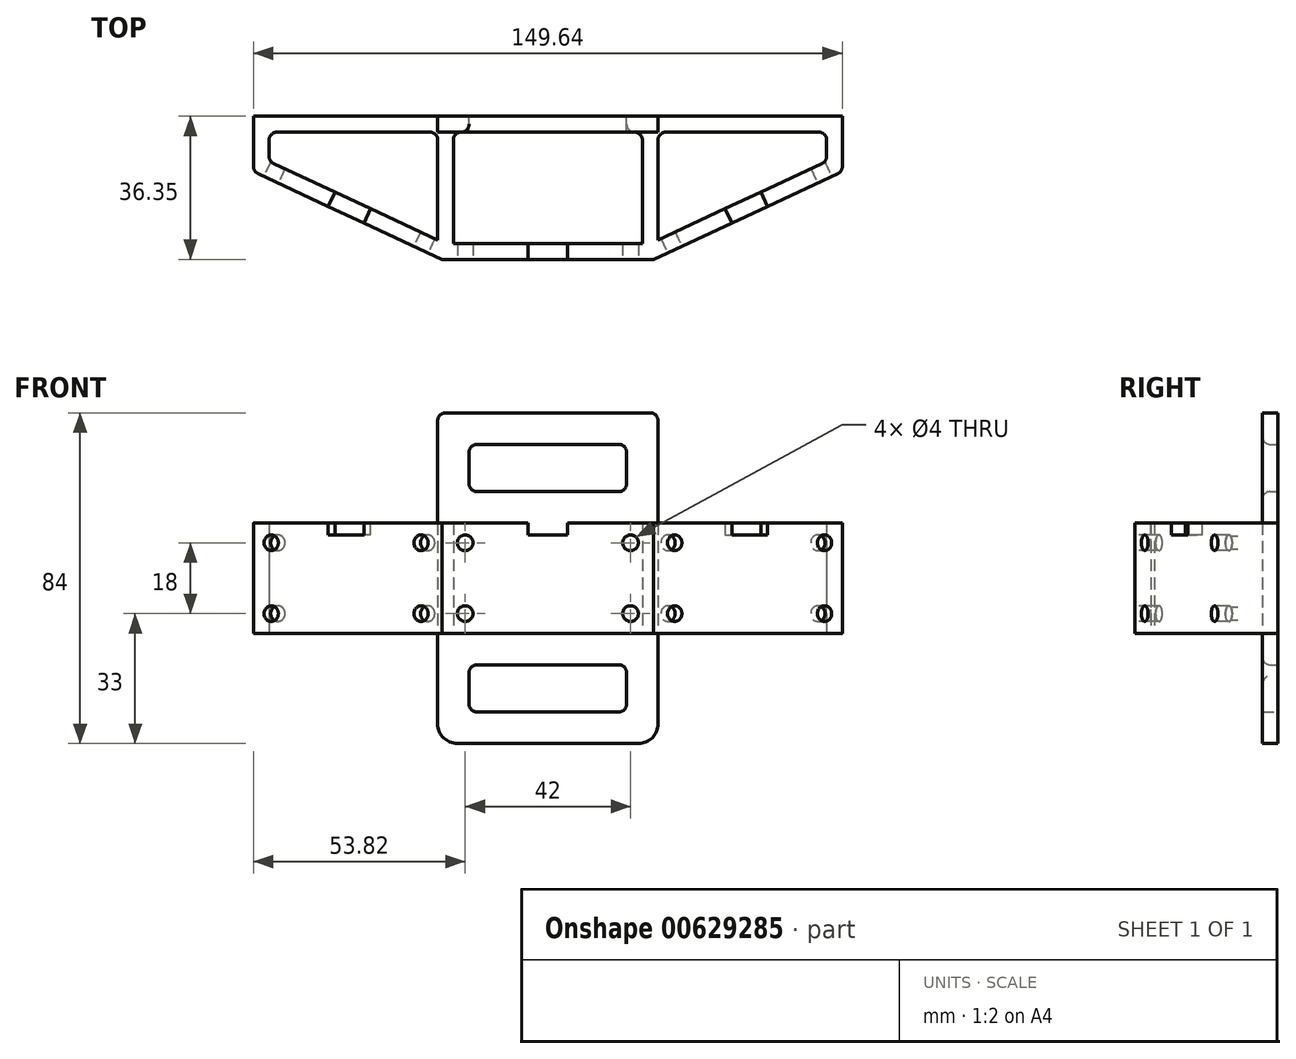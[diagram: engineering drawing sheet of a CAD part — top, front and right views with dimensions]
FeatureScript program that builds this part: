
annotation { "Feature Type Name" : "Feature", "Feature Type Description" : "" }
export const myFeature = defineFeature(function(context is Context, id is Id, definition is map)
    precondition{}
    {
        {
            var Q0;
            Q0=qCreatedBy(makeId("Top.planeOp"),FACE);
            var sketch = newSketch(context, id + "F0", { "sketchPlane" : qUnion([Q0])});
            skLineSegment(sketch, "E0", {"start": v(24, -117.28) * mm, "end": v(0, -117.28) * mm});
            skLineSegment(sketch, "E1", {"start": v(-28, -116.35) * mm, "end": v(-70.82, -96.38) * mm});
            skLineSegment(sketch, "E2", {"start": v(28, -116.35) * mm, "end": v(70.82, -96.38) * mm});
            skPoint(sketch, "E3.endSnap0", {"position": v(0, -117.28) * mm});
            skLineSegment(sketch, "E4", {"start": v(74.82, -98.93) * mm, "end": v(26.89, -121.28) * mm});
            skLineSegment(sketch, "E5", {"start": v(0, -121.28) * mm, "end": v(26.89, -121.28) * mm});
            skLineSegment(sketch, "E6", {"start": v(0, -121.28) * mm, "end": v(-26.89, -121.28) * mm});
            skLineSegment(sketch, "E7", {"start": v(-74.82, -98.93) * mm, "end": v(-26.89, -121.28) * mm});
            skPoint(sketch, "E3.start.orphan", {"position": v(0, -117.28) * mm});
            skLineSegment(sketch, "E8", {"start": v(74.82, -98.93) * mm, "end": v(74.82, -88.93) * mm});
            skLineSegment(sketch, "E9", {"start": v(70.82, -88.93) * mm, "end": v(70.82, -96.38) * mm});
            skLineSegment(sketch, "E10", {"start": v(-74.82, -98.93) * mm, "end": v(-74.82, -88.93) * mm});
            skLineSegment(sketch, "E11", {"start": v(-70.82, -88.93) * mm, "end": v(-70.82, -96.38) * mm});
            skLineSegment(sketch, "E12", {"start": v(-74.82, -88.93) * mm, "end": v(-74.82, -84.93) * mm});
            skLineSegment(sketch, "E13", {"start": v(74.82, -88.93) * mm, "end": v(74.82, -84.93) * mm});
            skLineSegment(sketch, "E14", {"start": v(74.82, -84.93) * mm, "end": v(-74.82, -84.93) * mm});
            skLineSegment(sketch, "E15", {"start": v(-26, -84.93) * mm, "end": v(-24, -84.93) * mm});
            skLineSegment(sketch, "E16", {"start": v(-24, -88.93) * mm, "end": v(-24, -117.28) * mm});
            skLineSegment(sketch, "E17", {"start": v(-26, -84.93) * mm, "end": v(-28, -84.93) * mm});
            skLineSegment(sketch, "E18", {"start": v(-28, -88.93) * mm, "end": v(-28, -116.35) * mm});
            skLineSegment(sketch, "E19", {"start": v(26, -84.93) * mm, "end": v(28, -84.93) * mm});
            skLineSegment(sketch, "E20", {"start": v(28, -88.93) * mm, "end": v(28, -116.35) * mm});
            skLineSegment(sketch, "E21", {"start": v(26, -84.93) * mm, "end": v(24, -84.93) * mm});
            skLineSegment(sketch, "E22", {"start": v(24, -88.93) * mm, "end": v(24, -117.28) * mm});
            skLineSegment(sketch, "E23.trimOffspring", {"start": v(28, -88.93) * mm, "end": v(70.82, -88.93) * mm});
            skLineSegment(sketch, "E24", {"start": v(24, -88.93) * mm, "end": v(-24, -88.93) * mm});
            skPoint(sketch, "E25.orphan", {"position": v(26, -117.28) * mm});
            skLineSegment(sketch, "E26", {"start": v(-28, -88.93) * mm, "end": v(-70.82, -88.93) * mm});
            skPoint(sketch, "E27.orphan", {"position": v(-26, -117.28) * mm});
            skLineSegment(sketch, "E28", {"start": v(0, -117.28) * mm, "end": v(-24, -117.28) * mm});
            skSolve(sketch);
        }
        {
            var Q0;
            Q0 = qSketchRegion(id + "F0", true);
            extrude(context, id + "F1", {"entities" : qUnion([Q0]), "depth" : 28 * mm, "offsetDistance" : 25 * mm});
        }
        {
            var Q0;
            Q0=makeQuery(id+"F1.opExtrude","CAP_FACE",FACE,{"disambiguationData":[OSD([sQuery(id+"F0.wireOp",EDGE,"E0"),sQuery(id+"F0.wireOp",EDGE,"E1"),sQuery(id+"F0.wireOp",EDGE,"E2"),sQuery(id+"F0.wireOp",EDGE,"E4"),sQuery(id+"F0.wireOp",EDGE,"E5"),sQuery(id+"F0.wireOp",EDGE,"E6"),sQuery(id+"F0.wireOp",EDGE,"E7"),sQuery(id+"F0.wireOp",EDGE,"E8"),sQuery(id+"F0.wireOp",EDGE,"E9"),sQuery(id+"F0.wireOp",EDGE,"E10"),sQuery(id+"F0.wireOp",EDGE,"E11"),sQuery(id+"F0.wireOp",EDGE,"E12"),sQuery(id+"F0.wireOp",EDGE,"E13"),sQuery(id+"F0.wireOp",EDGE,"E14"),sQuery(id+"F0.wireOp",EDGE,"E15"),sQuery(id+"F0.wireOp",EDGE,"E16"),sQuery(id+"F0.wireOp",EDGE,"E17"),sQuery(id+"F0.wireOp",EDGE,"E18"),sQuery(id+"F0.wireOp",EDGE,"E19"),sQuery(id+"F0.wireOp",EDGE,"E20"),sQuery(id+"F0.wireOp",EDGE,"E21"),sQuery(id+"F0.wireOp",EDGE,"E22"),sQuery(id+"F0.wireOp",EDGE,"E23.trimOffspring"),sQuery(id+"F0.wireOp",EDGE,"E24"),sQuery(id+"F0.wireOp",EDGE,"E26"),sQuery(id+"F0.wireOp",EDGE,"E28")])],"isStart":false});
            var sketch = newSketch(context, id + "F2", { "sketchPlane" : qUnion([Q0])});
            skLineSegment(sketch, "E29", {"start": v(28, -88.93) * mm, "end": v(28, -84.93) * mm});
            skLineSegment(sketch, "E30", {"start": v(-28, -88.93) * mm, "end": v(-28, -84.93) * mm});
            skLineSegment(sketch, "E31", {"start": v(-28, -84.93) * mm, "end": v(28, -84.93) * mm});
            skLineSegment(sketch, "E32", {"start": v(-28, -88.93) * mm, "end": v(28, -88.93) * mm});
            skSolve(sketch);
        }
        {
            var Q0;
            Q0 = qSketchRegion(id + "F2", true);
            extrude(context, id + "F3", {"entities" : qUnion([Q0]), "operationType" : NewBodyOperationType.ADD, "depth" : 28 * mm, "offsetDistance" : 25 * mm});
        }
        {
            var Q0;
            Q0=makeQuery(id+"F1.opExtrude","CAP_FACE",FACE,{"disambiguationData":[OSD([sQuery(id+"F0.wireOp",EDGE,"E0"),sQuery(id+"F0.wireOp",EDGE,"E1"),sQuery(id+"F0.wireOp",EDGE,"E2"),sQuery(id+"F0.wireOp",EDGE,"E4"),sQuery(id+"F0.wireOp",EDGE,"E5"),sQuery(id+"F0.wireOp",EDGE,"E6"),sQuery(id+"F0.wireOp",EDGE,"E7"),sQuery(id+"F0.wireOp",EDGE,"E8"),sQuery(id+"F0.wireOp",EDGE,"E9"),sQuery(id+"F0.wireOp",EDGE,"E10"),sQuery(id+"F0.wireOp",EDGE,"E11"),sQuery(id+"F0.wireOp",EDGE,"E12"),sQuery(id+"F0.wireOp",EDGE,"E13"),sQuery(id+"F0.wireOp",EDGE,"E14"),sQuery(id+"F0.wireOp",EDGE,"E15"),sQuery(id+"F0.wireOp",EDGE,"E16"),sQuery(id+"F0.wireOp",EDGE,"E17"),sQuery(id+"F0.wireOp",EDGE,"E18"),sQuery(id+"F0.wireOp",EDGE,"E19"),sQuery(id+"F0.wireOp",EDGE,"E20"),sQuery(id+"F0.wireOp",EDGE,"E21"),sQuery(id+"F0.wireOp",EDGE,"E22"),sQuery(id+"F0.wireOp",EDGE,"E23.trimOffspring"),sQuery(id+"F0.wireOp",EDGE,"E24"),sQuery(id+"F0.wireOp",EDGE,"E26"),sQuery(id+"F0.wireOp",EDGE,"E28")])],"isStart":true});
            var sketch = newSketch(context, id + "F4", { "sketchPlane" : qUnion([Q0])});
            skLineSegment(sketch, "E33", {"start": v(-28, 88.93) * mm, "end": v(-28, 84.93) * mm});
            skLineSegment(sketch, "E34", {"start": v(28, 88.93) * mm, "end": v(28, 84.93) * mm});
            skLineSegment(sketch, "E35", {"start": v(28, 84.93) * mm, "end": v(-28, 84.93) * mm});
            skLineSegment(sketch, "E36", {"start": v(28, 88.93) * mm, "end": v(-28, 88.93) * mm});
            skSolve(sketch);
        }
        {
            var Q0;
            Q0 = qSketchRegion(id + "F4", true);
            extrude(context, id + "F5", {"entities" : qUnion([Q0]), "operationType" : NewBodyOperationType.ADD, "depth" : 28 * mm, "offsetDistance" : 25 * mm});
        }
        {
            var Q0;
            Q0=makeQuery(id+"F5.boolean.opBoolean","MERGE",FACE,{"derivedFrom":[makeQuery(id+"F3.boolean.opBoolean","MERGE",FACE,{"derivedFrom":[makeQuery(id+"F1.opExtrude","SWEPT_FACE",FACE,{"disambiguationData":[OSD([sQuery(id+"F0.wireOp",EDGE,"E14"),sQuery(id+"F0.wireOp",EDGE,"E15"),sQuery(id+"F0.wireOp",EDGE,"E17"),sQuery(id+"F0.wireOp",EDGE,"E19"),sQuery(id+"F0.wireOp",EDGE,"E21")])]}),makeQuery(id+"F3.opExtrude","SWEPT_FACE",FACE,{"disambiguationData":[OSD([sQuery(id+"F2.wireOp",EDGE,"E31")])]})]}),makeQuery(id+"F5.opExtrude","SWEPT_FACE",FACE,{"disambiguationData":[OSD([sQuery(id+"F4.wireOp",EDGE,"E35")])]})]});
            var sketch = newSketch(context, id + "F6", { "sketchPlane" : qUnion([Q0])});
            skLineSegment(sketch, "E37", {"start": v(0, -28) * mm, "end": v(0, -20) * mm});
            skLineSegment(sketch, "E38", {"start": v(0, -20) * mm, "end": v(20, -20) * mm});
            skLineSegment(sketch, "E39", {"start": v(20, -20) * mm, "end": v(20, -8) * mm});
            skLineSegment(sketch, "E40", {"start": v(20, -8) * mm, "end": v(-20, -8) * mm});
            skLineSegment(sketch, "E41", {"start": v(-20, -8) * mm, "end": v(-20, -20) * mm});
            skLineSegment(sketch, "E42", {"start": v(0, -20) * mm, "end": v(-20, -20) * mm});
            skLineSegment(sketch, "E43", {"start": v(0, 56) * mm, "end": v(0, 48) * mm});
            skPoint(sketch, "E43.endSnap0", {"position": v(0, 56) * mm});
            skLineSegment(sketch, "E44", {"start": v(0, 48) * mm, "end": v(-20, 48) * mm});
            skLineSegment(sketch, "E45", {"start": v(-20, 48) * mm, "end": v(-20, 36) * mm});
            skLineSegment(sketch, "E46", {"start": v(-20, 36) * mm, "end": v(20, 36) * mm});
            skLineSegment(sketch, "E47", {"start": v(20, 36) * mm, "end": v(20, 48) * mm});
            skLineSegment(sketch, "E48", {"start": v(20, 48) * mm, "end": v(0, 48) * mm});
            skSolve(sketch);
        }
        {
            var Q0;
            Q0=makeQuery(id+"F6.imprint","IMPRINT",FACE,{"disambiguationData":[TD([[makeQuery(id+"F6.imprint","IMPRINT",EDGE,{"derivedFrom":sQuery(id+"F6.wireOp",EDGE,"E38")}),1.0]])]});
            var Q1;
            Q1=makeQuery(id+"F6.imprint","IMPRINT",FACE,{"disambiguationData":[TD([[makeQuery(id+"F6.imprint","IMPRINT",EDGE,{"derivedFrom":sQuery(id+"F6.wireOp",EDGE,"E44")}),1.0]])]});
            extrude(context, id + "F7", {"entities" : qUnion([Q0, Q1]), "operationType" : NewBodyOperationType.REMOVE, "oppositeDirection" : true, "depth" : 25 * mm, "offsetDistance" : 25 * mm});
        }
        {
            var Q0;
            Q0=makeQuery(id+"F1.opExtrude","SWEPT_FACE",FACE,{"disambiguationData":[OSD([sQuery(id+"F0.wireOp",EDGE,"E5"),sQuery(id+"F0.wireOp",EDGE,"E6")])]});
            var sketch = newSketch(context, id + "F8", { "sketchPlane" : qUnion([Q0])});
            skLineSegment(sketch, "E49", {"start": v(0, 0) * mm, "end": v(0, 28) * mm});
            skLineSegment(sketch, "E50", {"start": v(0, 14) * mm, "end": v(21, 14) * mm});
            skLineSegment(sketch, "E51", {"start": v(21, 14) * mm, "end": v(21, 23) * mm});
            skLineSegment(sketch, "E52", {"start": v(21, 14) * mm, "end": v(21, 5) * mm});
            skLineSegment(sketch, "E53", {"start": v(0, 14) * mm, "end": v(-21, 14) * mm});
            skLineSegment(sketch, "E54", {"start": v(-21, 14) * mm, "end": v(-21, 23) * mm});
            skLineSegment(sketch, "E55", {"start": v(-21, 14) * mm, "end": v(-21, 5) * mm});
            skLineSegment(sketch, "E56", {"start": v(0, 28) * mm, "end": v(-5, 28) * mm});
            skLineSegment(sketch, "E57", {"start": v(-5, 28) * mm, "end": v(-5, 25) * mm});
            skLineSegment(sketch, "E58", {"start": v(-5, 25) * mm, "end": v(5, 25) * mm});
            skLineSegment(sketch, "E59", {"start": v(5, 25) * mm, "end": v(5, 28) * mm});
            skCircle(sketch, "E60", {"center": v(-21, 23) * mm, "radius": 2 * mm});
            skCircle(sketch, "E61", {"center": v(-21, 5) * mm, "radius": 2 * mm});
            skCircle(sketch, "E62", {"center": v(21, 23) * mm, "radius": 2 * mm});
            skCircle(sketch, "E63", {"center": v(21, 5) * mm, "radius": 2 * mm});
            skSolve(sketch);
        }
        {
            var Q0;
            Q0 = qSketchRegion(id + "F8", true);
            var Q1;
            {var subQ5=sQuery(id+"F8.wireOp",EDGE,"E59");Q1=makeQuery(id+"F8.imprint","IMPRINT",FACE,{"disambiguationData":[TD([[makeQuery(id+"F8.imprint","IMPRINT",EDGE,{"derivedFrom":subQ5}),1.0]])]});}
            extrude(context, id + "F9", {"entities" : qUnion([Q0, Q1]), "operationType" : NewBodyOperationType.REMOVE, "oppositeDirection" : true, "depth" : 25 * mm, "offsetDistance" : 25 * mm});
        }
        {
            var Q0;
            Q0=makeQuery(id+"F1.opExtrude","SWEPT_FACE",FACE,{"disambiguationData":[OSD([sQuery(id+"F0.wireOp",EDGE,"E4")])]});
            var sketch = newSketch(context, id + "F10", { "sketchPlane" : qUnion([Q0])});
            skLineSegment(sketch, "E64", {"start": v(0, 0) * mm, "end": v(0, 28) * mm});
            skLineSegment(sketch, "E65", {"start": v(0, 28) * mm, "end": v(-5, 28) * mm});
            skLineSegment(sketch, "E66", {"start": v(-5, 28) * mm, "end": v(-5, 25) * mm});
            skLineSegment(sketch, "E67", {"start": v(-5, 25) * mm, "end": v(5, 25) * mm});
            skLineSegment(sketch, "E68", {"start": v(5, 25) * mm, "end": v(5, 28) * mm});
            skLineSegment(sketch, "E69", {"start": v(0, 14) * mm, "end": v(-21, 14) * mm});
            skPoint(sketch, "E69.endSnap0", {"position": v(0, 14) * mm});
            skLineSegment(sketch, "E70", {"start": v(-21, 14) * mm, "end": v(-21, 23) * mm});
            skLineSegment(sketch, "E71", {"start": v(-21, 14) * mm, "end": v(-21, 5) * mm});
            skLineSegment(sketch, "E72", {"start": v(0, 14) * mm, "end": v(21, 14) * mm});
            skLineSegment(sketch, "E73", {"start": v(21, 14) * mm, "end": v(21, 23) * mm});
            skLineSegment(sketch, "E74", {"start": v(21, 14) * mm, "end": v(21, 5) * mm});
            skCircle(sketch, "E75", {"center": v(-21, 23) * mm, "radius": 2 * mm});
            skCircle(sketch, "E76", {"center": v(-21, 5) * mm, "radius": 2 * mm});
            skCircle(sketch, "E77", {"center": v(21, 23) * mm, "radius": 2 * mm});
            skCircle(sketch, "E78", {"center": v(21, 5) * mm, "radius": 2 * mm});
            skSolve(sketch);
        }
        {
            var Q0;
            Q0 = qSketchRegion(id + "F10", true);
            var Q1;
            {var subQ5=sQuery(id+"F10.wireOp",EDGE,"E68");Q1=makeQuery(id+"F10.imprint","IMPRINT",FACE,{"disambiguationData":[TD([[makeQuery(id+"F10.imprint","IMPRINT",EDGE,{"derivedFrom":subQ5}),1.0]])]});}
            extrude(context, id + "F11", {"entities" : qUnion([Q0, Q1]), "operationType" : NewBodyOperationType.REMOVE, "oppositeDirection" : true, "depth" : 4 * mm, "offsetDistance" : 25 * mm});
        }
        {
            var Q0;
            Q0=makeQuery(id+"F1.opExtrude","SWEPT_FACE",FACE,{"disambiguationData":[OSD([sQuery(id+"F0.wireOp",EDGE,"E7")])]});
            var sketch = newSketch(context, id + "F12", { "sketchPlane" : qUnion([Q0])});
            skLineSegment(sketch, "E79", {"start": v(-26, 14) * mm, "end": v(26.89, 14) * mm});
            skLineSegment(sketch, "E80", {"start": v(0, 14) * mm, "end": v(0, 28) * mm});
            skLineSegment(sketch, "E81", {"start": v(0, 14) * mm, "end": v(0, 5) * mm});
            skLineSegment(sketch, "E82", {"start": v(0, 5) * mm, "end": v(21, 5) * mm});
            skLineSegment(sketch, "E83", {"start": v(0, 5) * mm, "end": v(-21, 5) * mm});
            skLineSegment(sketch, "E84", {"start": v(0, 14) * mm, "end": v(0, 23) * mm});
            skLineSegment(sketch, "E85", {"start": v(0, 23) * mm, "end": v(21, 23) * mm});
            skLineSegment(sketch, "E86", {"start": v(0, 23) * mm, "end": v(-21, 23) * mm});
            skLineSegment(sketch, "E87", {"start": v(0, 28) * mm, "end": v(-5, 28) * mm});
            skLineSegment(sketch, "E88", {"start": v(-5, 28) * mm, "end": v(-5, 25) * mm});
            skLineSegment(sketch, "E89", {"start": v(-5, 25) * mm, "end": v(5, 25) * mm});
            skLineSegment(sketch, "E90", {"start": v(5, 25) * mm, "end": v(5, 28) * mm});
            skCircle(sketch, "E91", {"center": v(-21, 23) * mm, "radius": 2 * mm});
            skCircle(sketch, "E92", {"center": v(-21, 5) * mm, "radius": 2 * mm});
            skCircle(sketch, "E93", {"center": v(21, 23) * mm, "radius": 2 * mm});
            skCircle(sketch, "E94", {"center": v(21, 5) * mm, "radius": 2 * mm});
            skSolve(sketch);
        }
        {
            var Q0;
            Q0=makeQuery(id+"F12.imprint","IMPRINT",FACE,{"disambiguationData":[TD([[makeQuery(id+"F12.imprint","IMPRINT",EDGE,{"derivedFrom":sQuery(id+"F12.wireOp",EDGE,"E92")}),1.0]])]});
            var Q1;
            Q1=makeQuery(id+"F12.imprint","IMPRINT",FACE,{"disambiguationData":[TD([[makeQuery(id+"F12.imprint","IMPRINT",EDGE,{"derivedFrom":sQuery(id+"F12.wireOp",EDGE,"E93")}),1.0]])]});
            var Q2;
            Q2=makeQuery(id+"F12.imprint","IMPRINT",FACE,{"disambiguationData":[TD([[makeQuery(id+"F12.imprint","IMPRINT",EDGE,{"derivedFrom":sQuery(id+"F12.wireOp",EDGE,"E94")}),1.0]])]});
            var Q3;
            {var subQ0=sQuery(id+"F12.wireOp",EDGE,"E87");Q3=makeQuery(id+"F12.imprint","IMPRINT",FACE,{"disambiguationData":[TD([[makeQuery(id+"F12.imprint","IMPRINT",EDGE,{"derivedFrom":subQ0}),-1.0]])]});}
            var Q4;
            {var subQ5=sQuery(id+"F12.wireOp",EDGE,"E90");Q4=makeQuery(id+"F12.imprint","IMPRINT",FACE,{"disambiguationData":[TD([[makeQuery(id+"F12.imprint","IMPRINT",EDGE,{"derivedFrom":subQ5}),1.0]])]});}
            var Q5;
            Q5=makeQuery(id+"F12.imprint","IMPRINT",FACE,{"disambiguationData":[TD([[makeQuery(id+"F12.imprint","IMPRINT",EDGE,{"derivedFrom":sQuery(id+"F12.wireOp",EDGE,"E91")}),1.0]])]});
            extrude(context, id + "F13", {"entities" : qUnion([Q0, Q1, Q2, Q3, Q4, Q5]), "operationType" : NewBodyOperationType.REMOVE, "oppositeDirection" : true, "depth" : 4 * mm, "offsetDistance" : 25 * mm});
        }
        {
            var Q0;
            Q0=makeQuery(id+"F7.boolean.opBoolean","INTERSECT",EDGE,{"derivedFrom":[makeQuery(id+"F5.boolean.opBoolean","MERGE",FACE,{"derivedFrom":[makeQuery(id+"F3.boolean.opBoolean","MERGE",FACE,{"derivedFrom":[makeQuery(id+"F1.opExtrude","SWEPT_FACE",FACE,{"disambiguationData":[OSD([sQuery(id+"F0.wireOp",EDGE,"E24")])]}),makeQuery(id+"F3.opExtrude","SWEPT_FACE",FACE,{"disambiguationData":[OSD([sQuery(id+"F2.wireOp",EDGE,"E32")])]})]}),makeQuery(id+"F5.opExtrude","SWEPT_FACE",FACE,{"disambiguationData":[OSD([sQuery(id+"F4.wireOp",EDGE,"E36")])]})]}),makeQuery(id+"F7.opExtrude","SWEPT_FACE",FACE,{"disambiguationData":[OSD([sQuery(id+"F6.wireOp",EDGE,"E46")])]})]});
            var Q1;
            Q1=makeQuery(id+"F7.boolean.opBoolean","COPY",EDGE,{"derivedFrom":makeQuery(id+"F7.opExtrude","CAP_EDGE",EDGE,{"disambiguationData":[OSD([sQuery(id+"F6.wireOp",EDGE,"E46")])],"isStart":true})});
            var Q2;
            Q2=makeQuery(id+"F7.boolean.opBoolean","INTERSECT",EDGE,{"derivedFrom":[makeQuery(id+"F5.boolean.opBoolean","MERGE",FACE,{"derivedFrom":[makeQuery(id+"F3.boolean.opBoolean","MERGE",FACE,{"derivedFrom":[makeQuery(id+"F1.opExtrude","SWEPT_FACE",FACE,{"disambiguationData":[OSD([sQuery(id+"F0.wireOp",EDGE,"E24")])]}),makeQuery(id+"F3.opExtrude","SWEPT_FACE",FACE,{"disambiguationData":[OSD([sQuery(id+"F2.wireOp",EDGE,"E32")])]})]}),makeQuery(id+"F5.opExtrude","SWEPT_FACE",FACE,{"disambiguationData":[OSD([sQuery(id+"F4.wireOp",EDGE,"E36")])]})]}),makeQuery(id+"F7.opExtrude","SWEPT_FACE",FACE,{"disambiguationData":[OSD([sQuery(id+"F6.wireOp",EDGE,"E47")])]})]});
            var Q3;
            Q3=makeQuery(id+"F7.boolean.opBoolean","COPY",EDGE,{"derivedFrom":makeQuery(id+"F7.opExtrude","CAP_EDGE",EDGE,{"disambiguationData":[OSD([sQuery(id+"F6.wireOp",EDGE,"E47")])],"isStart":true})});
            var Q4;
            Q4=makeQuery(id+"F7.boolean.opBoolean","COPY",EDGE,{"derivedFrom":makeQuery(id+"F7.opExtrude","CAP_EDGE",EDGE,{"disambiguationData":[OSD([sQuery(id+"F6.wireOp",EDGE,"E45")])],"isStart":true})});
            var Q5;
            Q5=makeQuery(id+"F7.boolean.opBoolean","INTERSECT",EDGE,{"derivedFrom":[makeQuery(id+"F5.boolean.opBoolean","MERGE",FACE,{"derivedFrom":[makeQuery(id+"F3.boolean.opBoolean","MERGE",FACE,{"derivedFrom":[makeQuery(id+"F1.opExtrude","SWEPT_FACE",FACE,{"disambiguationData":[OSD([sQuery(id+"F0.wireOp",EDGE,"E24")])]}),makeQuery(id+"F3.opExtrude","SWEPT_FACE",FACE,{"disambiguationData":[OSD([sQuery(id+"F2.wireOp",EDGE,"E32")])]})]}),makeQuery(id+"F5.opExtrude","SWEPT_FACE",FACE,{"disambiguationData":[OSD([sQuery(id+"F4.wireOp",EDGE,"E36")])]})]}),makeQuery(id+"F7.opExtrude","SWEPT_FACE",FACE,{"disambiguationData":[OSD([sQuery(id+"F6.wireOp",EDGE,"E45")])]})]});
            var Q6;
            Q6=makeQuery(id+"F7.boolean.opBoolean","COPY",EDGE,{"derivedFrom":makeQuery(id+"F7.opExtrude","SWEPT_EDGE",EDGE,{"disambiguationData":[OSD([sQuery(id+"F6.wireOp",EDGE,"E45"),sQuery(id+"F6.wireOp",EDGE,"E46")])]})});
            var Q7;
            Q7=makeQuery(id+"F7.boolean.opBoolean","COPY",EDGE,{"derivedFrom":makeQuery(id+"F7.opExtrude","SWEPT_EDGE",EDGE,{"disambiguationData":[OSD([sQuery(id+"F6.wireOp",EDGE,"E46"),sQuery(id+"F6.wireOp",EDGE,"E47")])]})});
            var Q8;
            Q8=makeQuery(id+"F7.boolean.opBoolean","COPY",EDGE,{"derivedFrom":makeQuery(id+"F7.opExtrude","SWEPT_EDGE",EDGE,{"disambiguationData":[OSD([sQuery(id+"F6.wireOp",EDGE,"E47"),sQuery(id+"F6.wireOp",EDGE,"E48")])]})});
            var Q9;
            Q9=makeQuery(id+"F7.boolean.opBoolean","INTERSECT",EDGE,{"derivedFrom":[makeQuery(id+"F5.boolean.opBoolean","MERGE",FACE,{"derivedFrom":[makeQuery(id+"F3.boolean.opBoolean","MERGE",FACE,{"derivedFrom":[makeQuery(id+"F1.opExtrude","SWEPT_FACE",FACE,{"disambiguationData":[OSD([sQuery(id+"F0.wireOp",EDGE,"E24")])]}),makeQuery(id+"F3.opExtrude","SWEPT_FACE",FACE,{"disambiguationData":[OSD([sQuery(id+"F2.wireOp",EDGE,"E32")])]})]}),makeQuery(id+"F5.opExtrude","SWEPT_FACE",FACE,{"disambiguationData":[OSD([sQuery(id+"F4.wireOp",EDGE,"E36")])]})]}),makeQuery(id+"F7.opExtrude","SWEPT_FACE",FACE,{"disambiguationData":[OSD([sQuery(id+"F6.wireOp",EDGE,"E44"),sQuery(id+"F6.wireOp",EDGE,"E48")])]})]});
            var Q10;
            Q10=makeQuery(id+"F7.boolean.opBoolean","COPY",EDGE,{"derivedFrom":makeQuery(id+"F7.opExtrude","CAP_EDGE",EDGE,{"disambiguationData":[OSD([sQuery(id+"F6.wireOp",EDGE,"E44"),sQuery(id+"F6.wireOp",EDGE,"E48")])],"isStart":true})});
            var Q11;
            Q11=makeQuery(id+"F7.boolean.opBoolean","COPY",EDGE,{"derivedFrom":makeQuery(id+"F7.opExtrude","SWEPT_EDGE",EDGE,{"disambiguationData":[OSD([sQuery(id+"F6.wireOp",EDGE,"E44"),sQuery(id+"F6.wireOp",EDGE,"E45")])]})});
            var Q12;
            Q12=makeQuery(id+"F3.opExtrude","CAP_EDGE",EDGE,{"disambiguationData":[OSD([sQuery(id+"F2.wireOp",EDGE,"E30")])],"isStart":false});
            var Q13;
            Q13=makeQuery(id+"F3.opExtrude","CAP_EDGE",EDGE,{"disambiguationData":[OSD([sQuery(id+"F2.wireOp",EDGE,"E29")])],"isStart":false});
            fillet(context, id + "F14", {"entities" : qUnion([Q0, Q1, Q2, Q3, Q4, Q5, Q6, Q7, Q8, Q9, Q10, Q11, Q12, Q13]), "radius" : 2 * mm, "tangentPropagation" : true, "allowEdgeOverflow" : false});
        }
        {
            var Q0;
            Q0=makeQuery(id+"F1.opExtrude","SWEPT_EDGE",EDGE,{"disambiguationData":[OSD([sQuery(id+"F0.wireOp",EDGE,"E20"),sQuery(id+"F0.wireOp",EDGE,"E23.trimOffspring")])]});
            var Q1;
            Q1=makeQuery(id+"F1.opExtrude","SWEPT_EDGE",EDGE,{"disambiguationData":[OSD([sQuery(id+"F0.wireOp",EDGE,"E22"),sQuery(id+"F0.wireOp",EDGE,"E24")])]});
            var Q2;
            Q2=makeQuery(id+"F1.opExtrude","SWEPT_EDGE",EDGE,{"disambiguationData":[OSD([sQuery(id+"F0.wireOp",EDGE,"E16"),sQuery(id+"F0.wireOp",EDGE,"E24")])]});
            var Q3;
            Q3=makeQuery(id+"F1.opExtrude","SWEPT_EDGE",EDGE,{"disambiguationData":[OSD([sQuery(id+"F0.wireOp",EDGE,"E18"),sQuery(id+"F0.wireOp",EDGE,"E26")])]});
            var Q4;
            Q4=makeQuery(id+"F1.opExtrude","SWEPT_EDGE",EDGE,{"disambiguationData":[OSD([sQuery(id+"F0.wireOp",EDGE,"E9"),sQuery(id+"F0.wireOp",EDGE,"E23.trimOffspring")])]});
            var Q5;
            Q5=makeQuery(id+"F1.opExtrude","SWEPT_EDGE",EDGE,{"disambiguationData":[OSD([sQuery(id+"F0.wireOp",EDGE,"E2"),sQuery(id+"F0.wireOp",EDGE,"E9")])]});
            var Q6;
            Q6=makeQuery(id+"F1.opExtrude","SWEPT_EDGE",EDGE,{"disambiguationData":[OSD([sQuery(id+"F0.wireOp",EDGE,"E11"),sQuery(id+"F0.wireOp",EDGE,"E26")])]});
            var Q7;
            Q7=makeQuery(id+"F1.opExtrude","SWEPT_EDGE",EDGE,{"disambiguationData":[OSD([sQuery(id+"F0.wireOp",EDGE,"E1"),sQuery(id+"F0.wireOp",EDGE,"E11")])]});
            var Q8;
            Q8=makeQuery(id+"F1.opExtrude","SWEPT_EDGE",EDGE,{"disambiguationData":[OSD([sQuery(id+"F0.wireOp",EDGE,"E4"),sQuery(id+"F0.wireOp",EDGE,"E8")])]});
            var Q9;
            Q9=makeQuery(id+"F1.opExtrude","SWEPT_EDGE",EDGE,{"disambiguationData":[OSD([sQuery(id+"F0.wireOp",EDGE,"E7"),sQuery(id+"F0.wireOp",EDGE,"E10")])]});
            var Q10;
            Q10=makeQuery(id+"F7.boolean.opBoolean","COPY",EDGE,{"derivedFrom":makeQuery(id+"F7.opExtrude","SWEPT_EDGE",EDGE,{"disambiguationData":[OSD([sQuery(id+"F6.wireOp",EDGE,"E40"),sQuery(id+"F6.wireOp",EDGE,"E41")])]})});
            var Q11;
            Q11=makeQuery(id+"F7.boolean.opBoolean","INTERSECT",EDGE,{"derivedFrom":[makeQuery(id+"F5.boolean.opBoolean","MERGE",FACE,{"derivedFrom":[makeQuery(id+"F3.boolean.opBoolean","MERGE",FACE,{"derivedFrom":[makeQuery(id+"F1.opExtrude","SWEPT_FACE",FACE,{"disambiguationData":[OSD([sQuery(id+"F0.wireOp",EDGE,"E24")])]}),makeQuery(id+"F3.opExtrude","SWEPT_FACE",FACE,{"disambiguationData":[OSD([sQuery(id+"F2.wireOp",EDGE,"E32")])]})]}),makeQuery(id+"F5.opExtrude","SWEPT_FACE",FACE,{"disambiguationData":[OSD([sQuery(id+"F4.wireOp",EDGE,"E36")])]})]}),makeQuery(id+"F7.opExtrude","SWEPT_FACE",FACE,{"disambiguationData":[OSD([sQuery(id+"F6.wireOp",EDGE,"E40")])]})]});
            var Q12;
            Q12=makeQuery(id+"F7.boolean.opBoolean","COPY",EDGE,{"derivedFrom":makeQuery(id+"F7.opExtrude","CAP_EDGE",EDGE,{"disambiguationData":[OSD([sQuery(id+"F6.wireOp",EDGE,"E40")])],"isStart":true})});
            var Q13;
            Q13=makeQuery(id+"F7.boolean.opBoolean","COPY",EDGE,{"derivedFrom":makeQuery(id+"F7.opExtrude","SWEPT_EDGE",EDGE,{"disambiguationData":[OSD([sQuery(id+"F6.wireOp",EDGE,"E39"),sQuery(id+"F6.wireOp",EDGE,"E40")])]})});
            var Q14;
            Q14=makeQuery(id+"F7.boolean.opBoolean","COPY",EDGE,{"derivedFrom":makeQuery(id+"F7.opExtrude","SWEPT_EDGE",EDGE,{"disambiguationData":[OSD([sQuery(id+"F6.wireOp",EDGE,"E38"),sQuery(id+"F6.wireOp",EDGE,"E39")])]})});
            var Q15;
            Q15=makeQuery(id+"F7.boolean.opBoolean","COPY",EDGE,{"derivedFrom":makeQuery(id+"F7.opExtrude","SWEPT_EDGE",EDGE,{"disambiguationData":[OSD([sQuery(id+"F6.wireOp",EDGE,"E41"),sQuery(id+"F6.wireOp",EDGE,"E42")])]})});
            fillet(context, id + "F15", {"entities" : qUnion([Q0, Q1, Q2, Q3, Q4, Q5, Q6, Q7, Q8, Q9, Q10, Q11, Q12, Q13, Q14, Q15]), "radius" : 2 * mm, "tangentPropagation" : true, "allowEdgeOverflow" : false});
        }
        {
            var Q0;
            Q0=makeQuery(id+"F5.opExtrude","CAP_EDGE",EDGE,{"disambiguationData":[OSD([sQuery(id+"F4.wireOp",EDGE,"E33")])],"isStart":false});
            var Q1;
            Q1=makeQuery(id+"F5.opExtrude","CAP_EDGE",EDGE,{"disambiguationData":[OSD([sQuery(id+"F4.wireOp",EDGE,"E34")])],"isStart":false});
            fillet(context, id + "F16", {"entities" : qUnion([Q0, Q1]), "radius" : 5 * mm, "tangentPropagation" : true, "allowEdgeOverflow" : false});
        }
    });
